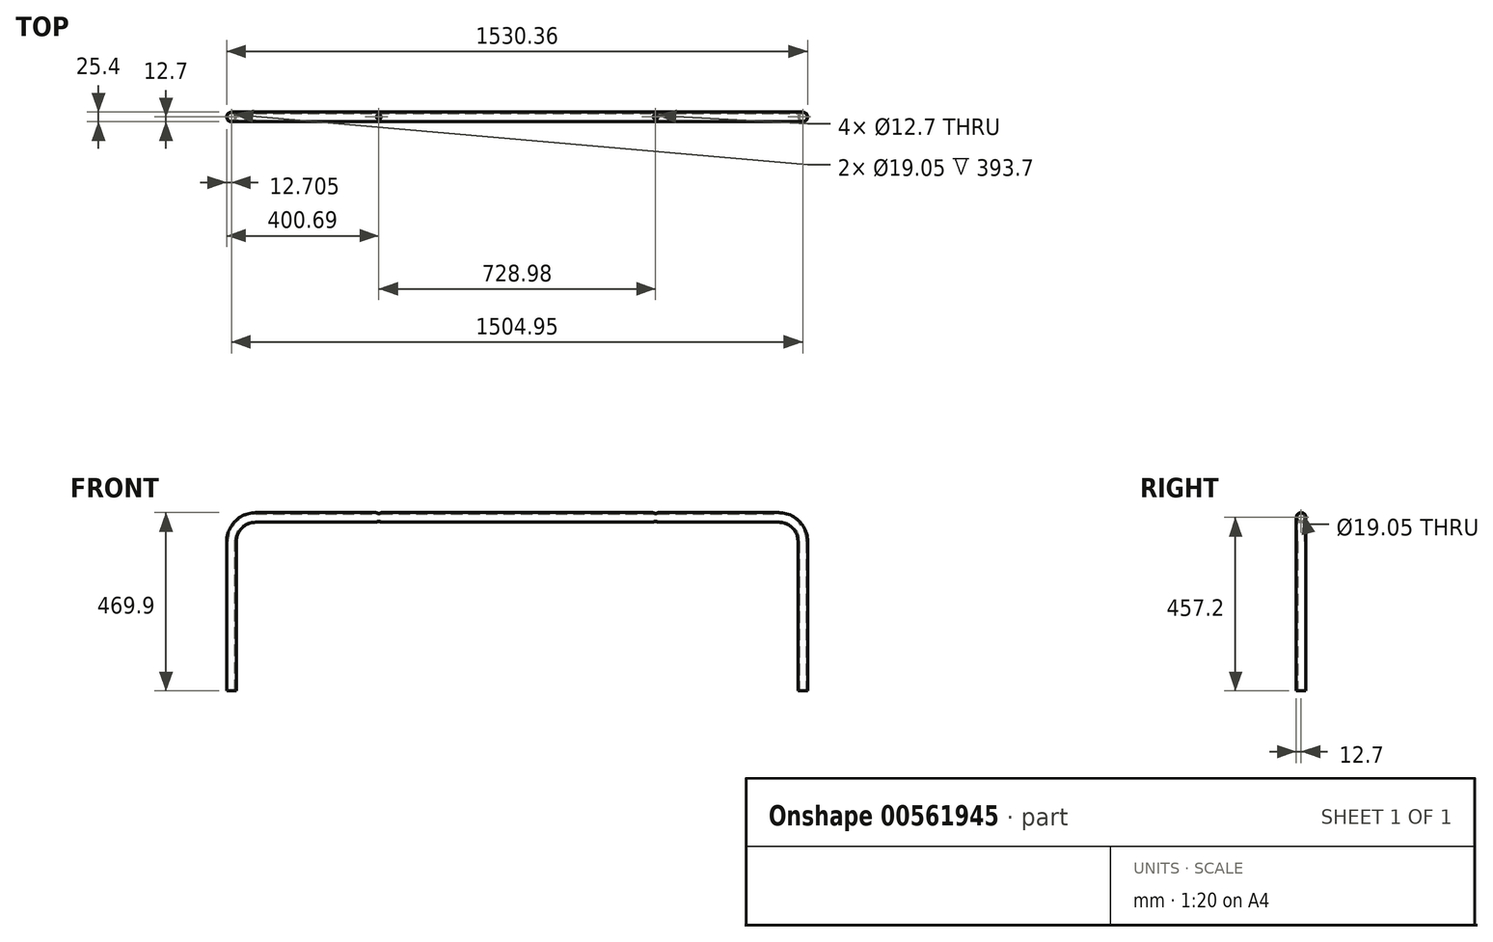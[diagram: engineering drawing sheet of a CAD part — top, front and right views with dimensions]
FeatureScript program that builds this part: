
annotation { "Feature Type Name" : "Feature", "Feature Type Description" : "" }
export const myFeature = defineFeature(function(context is Context, id is Id, definition is map)
    precondition{}
    {
        {
            var Q0;
            Q0=qCreatedBy(makeId("Front.planeOp"),FACE);
            var sketch = newSketch(context, id + "F0", { "sketchPlane" : qUnion([Q0])});
            skLineSegment(sketch, "E0", {"start": v(-752.48, 0) * mm, "end": v(752.48, 0) * mm, "construction": true});
            skLineSegment(sketch, "E1", {"start": v(0, 0) * mm, "end": v(0, 635) * mm, "construction": true});
            skLineSegment(sketch, "E2", {"start": v(-752.48, 0) * mm, "end": v(-752.48, 393.7) * mm});
            skLineSegment(sketch, "E3", {"start": v(752.48, 0) * mm, "end": v(752.48, 393.7) * mm});
            skLineSegment(sketch, "E4", {"start": v(-688.98, 457.2) * mm, "end": v(688.98, 457.2) * mm});
            skPoint(sketch, "E5.visualSharp", {"position": v(-752.48, 457.2) * mm});
            skArc(sketch, "E5.filletArc", {"start": v(-688.98, 457.2) * mm, "mid": v(-733.88, 438.6) * mm, "end": v(-752.48, 393.7) * mm});
            skPoint(sketch, "E6.visualSharp", {"position": v(752.48, 457.2) * mm});
            skArc(sketch, "E6.filletArc", {"start": v(752.48, 393.7) * mm, "mid": v(733.88, 438.6) * mm, "end": v(688.98, 457.2) * mm});
            skSolve(sketch);
        }
        {
            var Q0;
            Q0=qCreatedBy(makeId("Top.planeOp"),FACE);
            var sketch = newSketch(context, id + "F1", { "sketchPlane" : qUnion([Q0])});
            skCircle(sketch, "E7", {"center": v(-752.48, 0) * mm, "radius": 9.53 * mm});
            skCircle(sketch, "E8", {"center": v(-752.48, 0) * mm, "radius": 12.7 * mm});
            skSolve(sketch);
        }
        {
            var Q0;
            Q0=makeQuery(id+"F1.imprint","IMPRINT",FACE,{"disambiguationData":[TD([[makeQuery(id+"F1.imprint","IMPRINT",EDGE,{"derivedFrom":sQuery(id+"F1.wireOp",EDGE,"E7")}),-1.0]])]});
            var Q1;
            Q1=sQuery(id+"F1.wireOp",EDGE,"E8");
            var Q2;
            Q2=sQuery(id+"F1.wireOp",EDGE,"E7");
            var Q3;
            Q3 = qConstructionFilter(qBodyType(qCreatedBy(id + "F0" ,EDGE), BodyType.WIRE), ConstructionObject.NO);
            sweep(context, id + "F2", {"profiles" : qUnion([Q0]), "surfaceProfiles" : qUnion([Q1, Q2]), "path" : qUnion([Q3])});
        }
        {
            var Q0;
            Q0=qCreatedBy(makeId("Top.planeOp"),FACE);
            cPlane(context, id + "F3", {"entities" : qUnion([Q0]), "cplaneType" : CPlaneType.OFFSET, "offset" : 457.2 * mm, "width" : 152.4 * mm, "height" : 152.4 * mm});
        }
        {
            var Q0;
            Q0=qCreatedBy(id+"F3.planeOp",FACE);
            var sketch = newSketch(context, id + "F4", { "sketchPlane" : qUnion([Q0])});
            skCircle(sketch, "E9", {"center": v(-364.5, 0) * mm, "radius": 6.35 * mm});
            skCircle(sketch, "E10", {"center": v(364.5, 0) * mm, "radius": 6.35 * mm});
            skSolve(sketch);
        }
        {
            var Q0;
            Q0 = qSketchRegion(id + "F4", true);
            extrude(context, id + "F5", {"entities" : qUnion([Q0]), "operationType" : NewBodyOperationType.REMOVE, "oppositeDirection" : true, "depth" : 25.4 * mm, "offsetDistance" : 25.4 * mm, "symmetric" : true});
        }
    });
